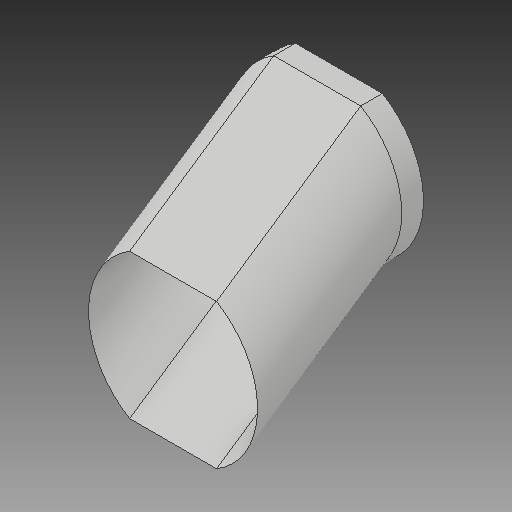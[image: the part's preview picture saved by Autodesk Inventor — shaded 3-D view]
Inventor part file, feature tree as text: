
AUTODESK INVENTOR PART (.ipt)
format: ipt  version: 2017 (Build 210142000, 142)  size: 123,392 bytes
history: native  units: in
note: dims shown in document units (in); Inventor stores cm internally (conversion verified against a paired STEP export)
features: sketch x2, extrude x1, plane x1, sweep x1, delete_face x1
ambient origin geometry x8: Origin, YZ Plane, XZ Plane, XY Plane, X Axis, Y Axis, Z Axis, Center Point
bodies: Solid1 (feature_tree)
feature tree (6):
  sketch  "Sketch1"  dims[d0=6.6667in d3=1.0in d4=0.0in d12=8.0in]
  extrude  "connecction top"  Depth=6.6667in
  plane  "Work Plane2"
  sweep  "ramp"
  delete_face  "Delete Face1"
  sketch  "Sketch6"  dims[d28=8.0in d45=0.0in d46=0.0in d65=0.8521in d66=4.0in d68=3.8873in d69=3.8873in d73=1.6458in d79=3.3333in]
